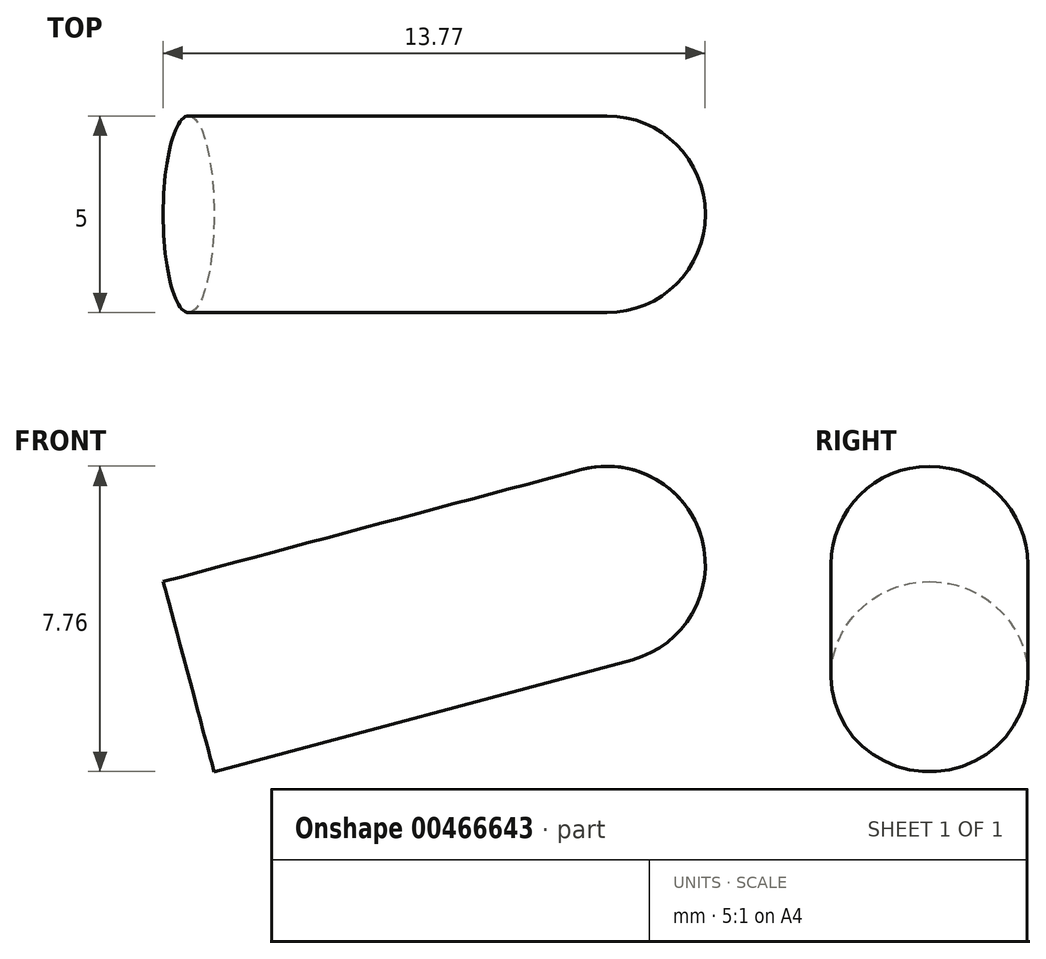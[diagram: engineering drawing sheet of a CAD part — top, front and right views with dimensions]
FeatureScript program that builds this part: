
annotation { "Feature Type Name" : "Feature", "Feature Type Description" : "" }
export const myFeature = defineFeature(function(context is Context, id is Id, definition is map)
    precondition{}
    {
        {
            var Q0;
            Q0=qCreatedBy(makeId("Front.planeOp"),FACE);
            var sketch = newSketch(context, id + "F0", { "sketchPlane" : qUnion([Q0])});
            skLineSegment(sketch, "E0", {"start": v(-11.55, 0) * mm, "end": v(11, 0) * mm, "construction": true});
            skLineSegment(sketch, "E1", {"start": v(-6.4, 2.5) * mm, "end": v(4.6, 2.5) * mm});
            skArc(sketch, "E2", {"start": v(7.1, 0) * mm, "mid": v(6.36, 1.77) * mm, "end": v(4.6, 2.5) * mm});
            skLineSegment(sketch, "E3", {"start": v(-6.4, 2.5) * mm, "end": v(-6.4, 0) * mm});
            skLineSegment(sketch, "E4", {"start": v(-6.4, 0) * mm, "end": v(7.1, 0) * mm});
            skSolve(sketch);
        }
        {
            var Q0;
            Q0=makeQuery(id+"F0.imprint","IMPRINT",FACE,{"disambiguationData":[TD([[makeQuery(id+"F0.imprint","IMPRINT",EDGE,{"derivedFrom":sQuery(id+"F0.wireOp",EDGE,"E1")}),-1.0]])]});
            var Q1;
            Q1=sQuery(id+"F0.wireOp",EDGE,"E0");
            revolve(context, id + "F1", {"entities" : qUnion([Q0]), "axis" : qUnion([Q1]), "revolveType" : RevolveType.FULL});
        }
        {
            var Q0;
            Q0=qCreatedBy(makeId("Right.planeOp"),FACE);
            var sketch = newSketch(context, id + "F2", { "sketchPlane" : qUnion([Q0])});
            skLineSegment(sketch, "E5", {"start": v(-79.9, 0) * mm, "end": v(80.75, 0) * mm, "construction": true});
            skSolve(sketch);
        }
        {
            var Q0;
            Q0=makeQuery(id+"F1.opRevolve","SWEPT_BODY",BODY,{"disambiguationData":[OSD([sQuery(id+"F0.wireOp",EDGE,"E1"),sQuery(id+"F0.wireOp",EDGE,"E2"),sQuery(id+"F0.wireOp",EDGE,"E3"),sQuery(id+"F0.wireOp",EDGE,"E4")])]});
            var Q1;
            Q1=sQuery(id+"F2.wireOp",EDGE,"E5");
            transform(context, id + "F3", {"entities" : qUnion([Q0]), "transformType" : TransformType.ROTATION, "transformAxis" : qUnion([Q1]), "angle" : 15 * degree, "oppositeDirection" : true, "makeCopy" : false});
        }
    });
